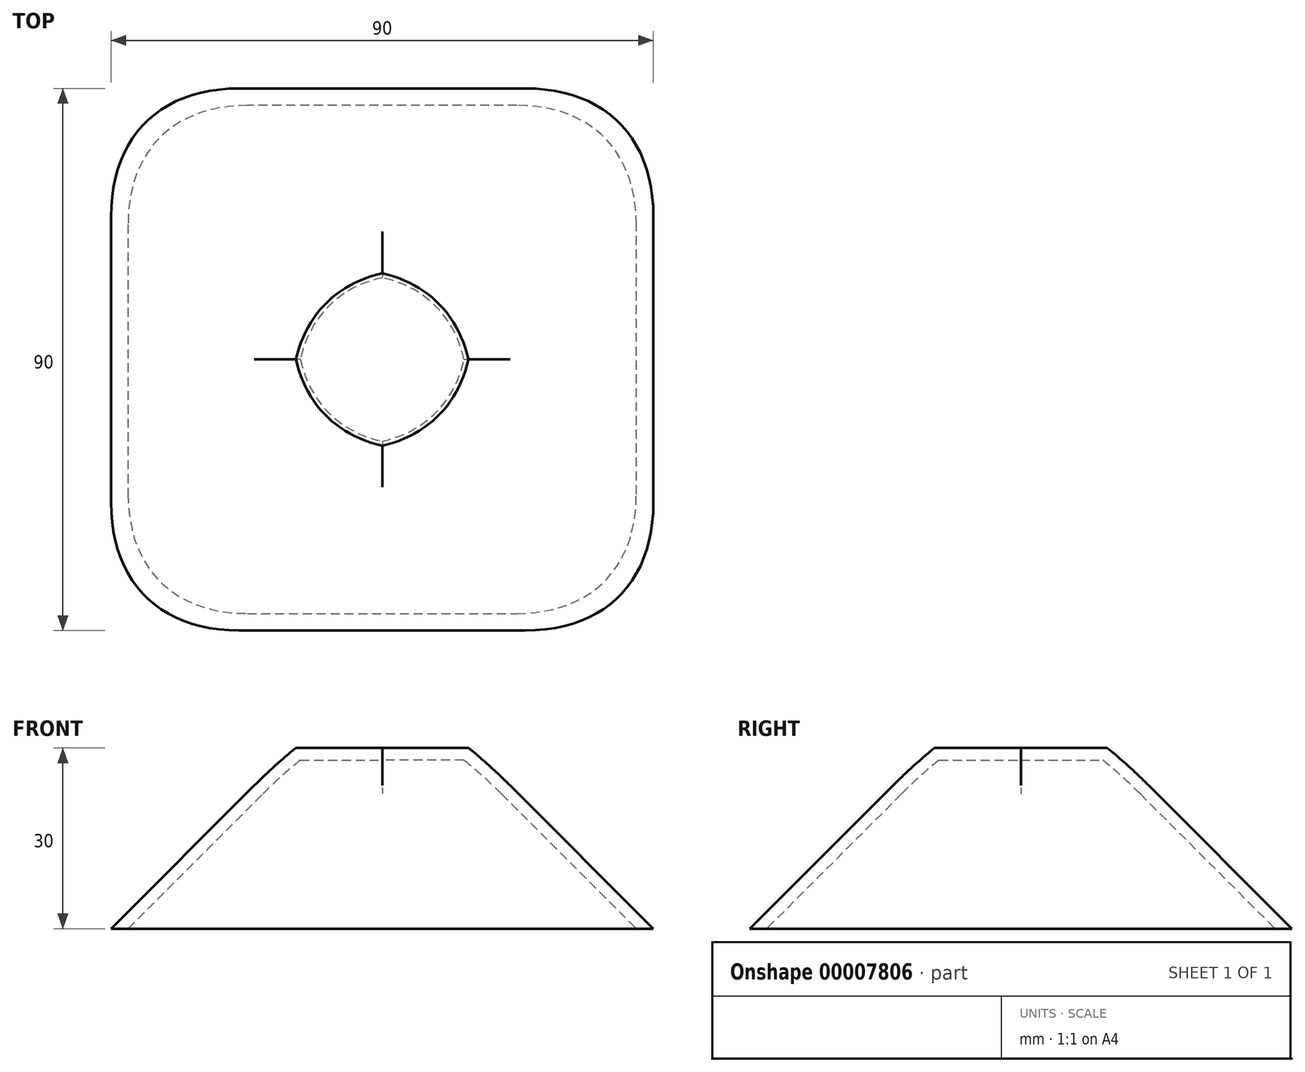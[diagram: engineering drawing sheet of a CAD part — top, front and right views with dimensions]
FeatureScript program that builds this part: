
annotation { "Feature Type Name" : "Feature", "Feature Type Description" : "" }
export const myFeature = defineFeature(function(context is Context, id is Id, definition is map)
    precondition{}
    {
        {
            var Q0;
            Q0=qCreatedBy(makeId("Top.planeOp"),FACE);
            var sketch = newSketch(context, id + "F0", { "sketchPlane" : qUnion([Q0])});
            skLineSegment(sketch, "E0.rect.bottom", {"start": v(-45, -45) * mm, "end": v(45, -45) * mm});
            skLineSegment(sketch, "E0.rect.top", {"start": v(-45, 45) * mm, "end": v(45, 45) * mm});
            skLineSegment(sketch, "E0.rect.left", {"start": v(-45, -45) * mm, "end": v(-45, 45) * mm});
            skLineSegment(sketch, "E0.rect.right", {"start": v(45, -45) * mm, "end": v(45, 45) * mm});
            skPoint(sketch, "E0.rect.middle", {"position": v(0, 0) * mm});
            skSolve(sketch);
        }
        {
            var Q0;
            Q0=makeQuery(id+"F0.imprint","IMPRINT",FACE,{"disambiguationData":[TD([[makeQuery(id+"F0.imprint","IMPRINT",EDGE,{"derivedFrom":sQuery(id+"F0.wireOp",EDGE,"E0.rect.bottom")}),1.0]])]});
            extrude(context, id + "F1", {"entities" : qUnion([Q0]), "depth" : 30 * mm});
        }
        {
            var Q0;
            Q0=makeQuery(id+"F1.opExtrude","CAP_EDGE",EDGE,{"disambiguationData":[OSD([sQuery(id+"F0.wireOp",EDGE,"E0.rect.right")])],"isStart":false});
            var Q1;
            Q1=makeQuery(id+"F1.opExtrude","CAP_EDGE",EDGE,{"disambiguationData":[OSD([sQuery(id+"F0.wireOp",EDGE,"E0.rect.bottom")])],"isStart":false});
            var Q2;
            Q2=makeQuery(id+"F1.opExtrude","CAP_EDGE",EDGE,{"disambiguationData":[OSD([sQuery(id+"F0.wireOp",EDGE,"E0.rect.left")])],"isStart":false});
            var Q3;
            Q3=makeQuery(id+"F1.opExtrude","CAP_EDGE",EDGE,{"disambiguationData":[OSD([sQuery(id+"F0.wireOp",EDGE,"E0.rect.top")])],"isStart":false});
            chamfer(context, id + "F2", {"entities" : qUnion([Q0, Q1, Q2, Q3]), "width" : 30 * mm, "tangentPropagation" : true});
        }
        {
            var Q0;
            Q0=makeQuery(id+"F2.opChamfer","BLEND_EDGE",EDGE,{"blendedFrom":[makeQuery(id+"F1.opExtrude","CAP_EDGE",EDGE,{"disambiguationData":[OSD([sQuery(id+"F0.wireOp",EDGE,"E0.rect.top")])],"isStart":false}),makeQuery(id+"F1.opExtrude","CAP_EDGE",EDGE,{"disambiguationData":[OSD([sQuery(id+"F0.wireOp",EDGE,"E0.rect.right")])],"isStart":false})],"blendedInto":[]});
            var Q1;
            Q1=makeQuery(id+"F2.opChamfer","BLEND_EDGE",EDGE,{"blendedFrom":[makeQuery(id+"F1.opExtrude","CAP_EDGE",EDGE,{"disambiguationData":[OSD([sQuery(id+"F0.wireOp",EDGE,"E0.rect.bottom")])],"isStart":false}),makeQuery(id+"F1.opExtrude","CAP_EDGE",EDGE,{"disambiguationData":[OSD([sQuery(id+"F0.wireOp",EDGE,"E0.rect.right")])],"isStart":false})],"blendedInto":[]});
            var Q2;
            Q2=makeQuery(id+"F2.opChamfer","BLEND_EDGE",EDGE,{"blendedFrom":[makeQuery(id+"F1.opExtrude","CAP_EDGE",EDGE,{"disambiguationData":[OSD([sQuery(id+"F0.wireOp",EDGE,"E0.rect.bottom")])],"isStart":false}),makeQuery(id+"F1.opExtrude","CAP_EDGE",EDGE,{"disambiguationData":[OSD([sQuery(id+"F0.wireOp",EDGE,"E0.rect.left")])],"isStart":false})],"blendedInto":[]});
            var Q3;
            Q3=makeQuery(id+"F2.opChamfer","BLEND_EDGE",EDGE,{"blendedFrom":[makeQuery(id+"F1.opExtrude","CAP_EDGE",EDGE,{"disambiguationData":[OSD([sQuery(id+"F0.wireOp",EDGE,"E0.rect.top")])],"isStart":false}),makeQuery(id+"F1.opExtrude","CAP_EDGE",EDGE,{"disambiguationData":[OSD([sQuery(id+"F0.wireOp",EDGE,"E0.rect.left")])],"isStart":false})],"blendedInto":[]});
            fillet(context, id + "F3", {"entities" : qUnion([Q0, Q1, Q2, Q3]), "radius" : 30 * mm, "tangentPropagation" : true, "allowEdgeOverflow" : false});
        }
        {
            var Q0;
            Q0=makeQuery(id+"F1.opExtrude","CAP_FACE",FACE,{"disambiguationData":[OSD([sQuery(id+"F0.wireOp",EDGE,"E0.rect.bottom"),sQuery(id+"F0.wireOp",EDGE,"E0.rect.top"),sQuery(id+"F0.wireOp",EDGE,"E0.rect.left"),sQuery(id+"F0.wireOp",EDGE,"E0.rect.right")])],"isStart":true});
            shell(context, id + "F4", {"entities" : qUnion([Q0]), "thickness" : 2 * mm});
        }
    });
